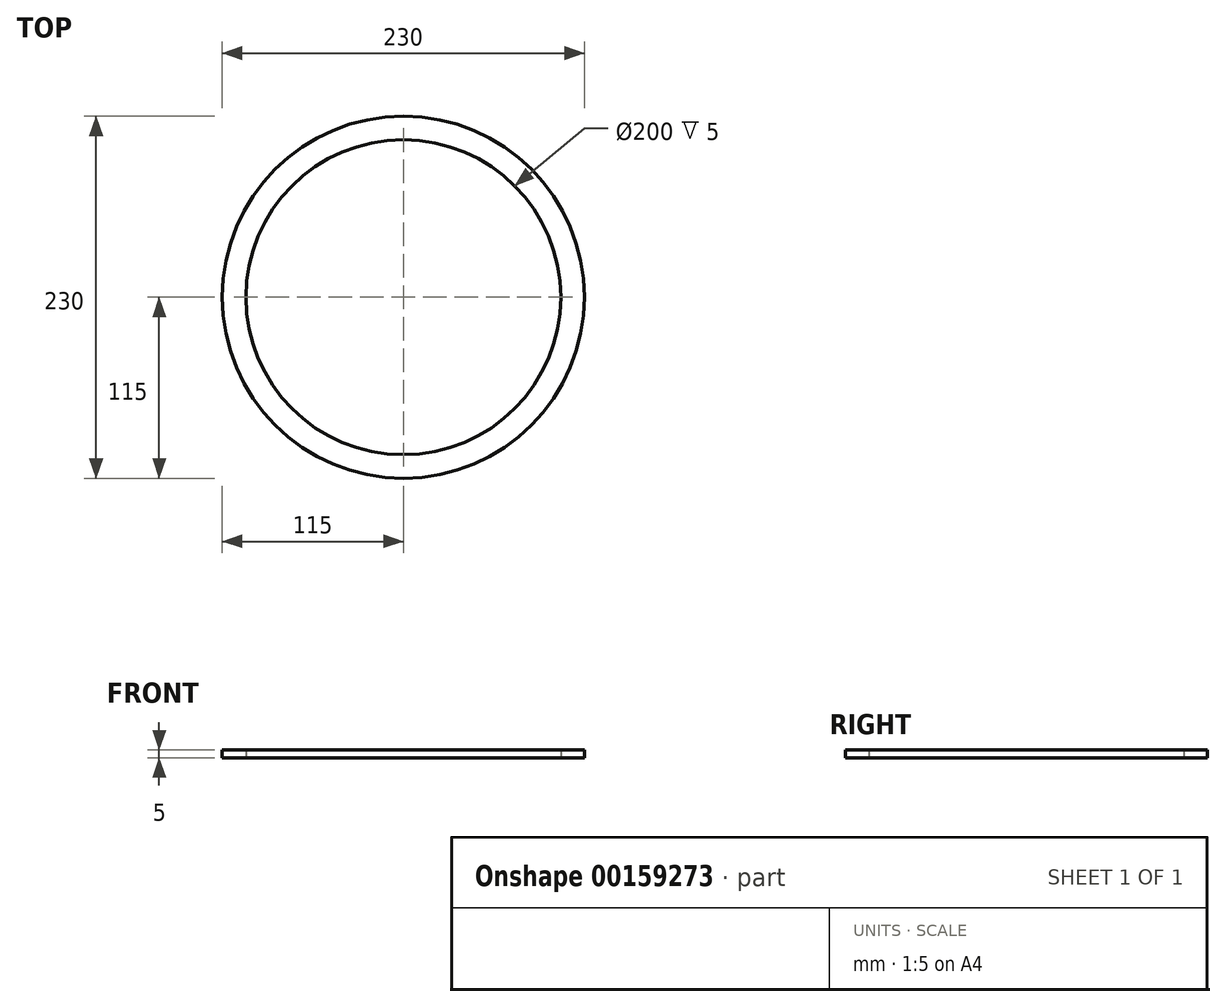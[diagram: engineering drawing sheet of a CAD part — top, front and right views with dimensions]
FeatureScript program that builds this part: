
annotation { "Feature Type Name" : "Feature", "Feature Type Description" : "" }
export const myFeature = defineFeature(function(context is Context, id is Id, definition is map)
    precondition{}
    {
        {
            var Q0;
            Q0=qCreatedBy(makeId("Top.planeOp"),FACE);
            var sketch = newSketch(context, id + "F0", { "sketchPlane" : qUnion([Q0])});
            skCircle(sketch, "E0", {"center": v(0, 0) * mm, "radius": 115 * mm});
            skCircle(sketch, "E1", {"center": v(0, 0) * mm, "radius": 100 * mm});
            skSolve(sketch);
        }
        {
            var Q0;
            Q0 = qSketchRegion(id + "F0", true);
            extrude(context, id + "F1", {"entities" : qUnion([Q0]), "depth" : 5 * mm});
        }
    });
